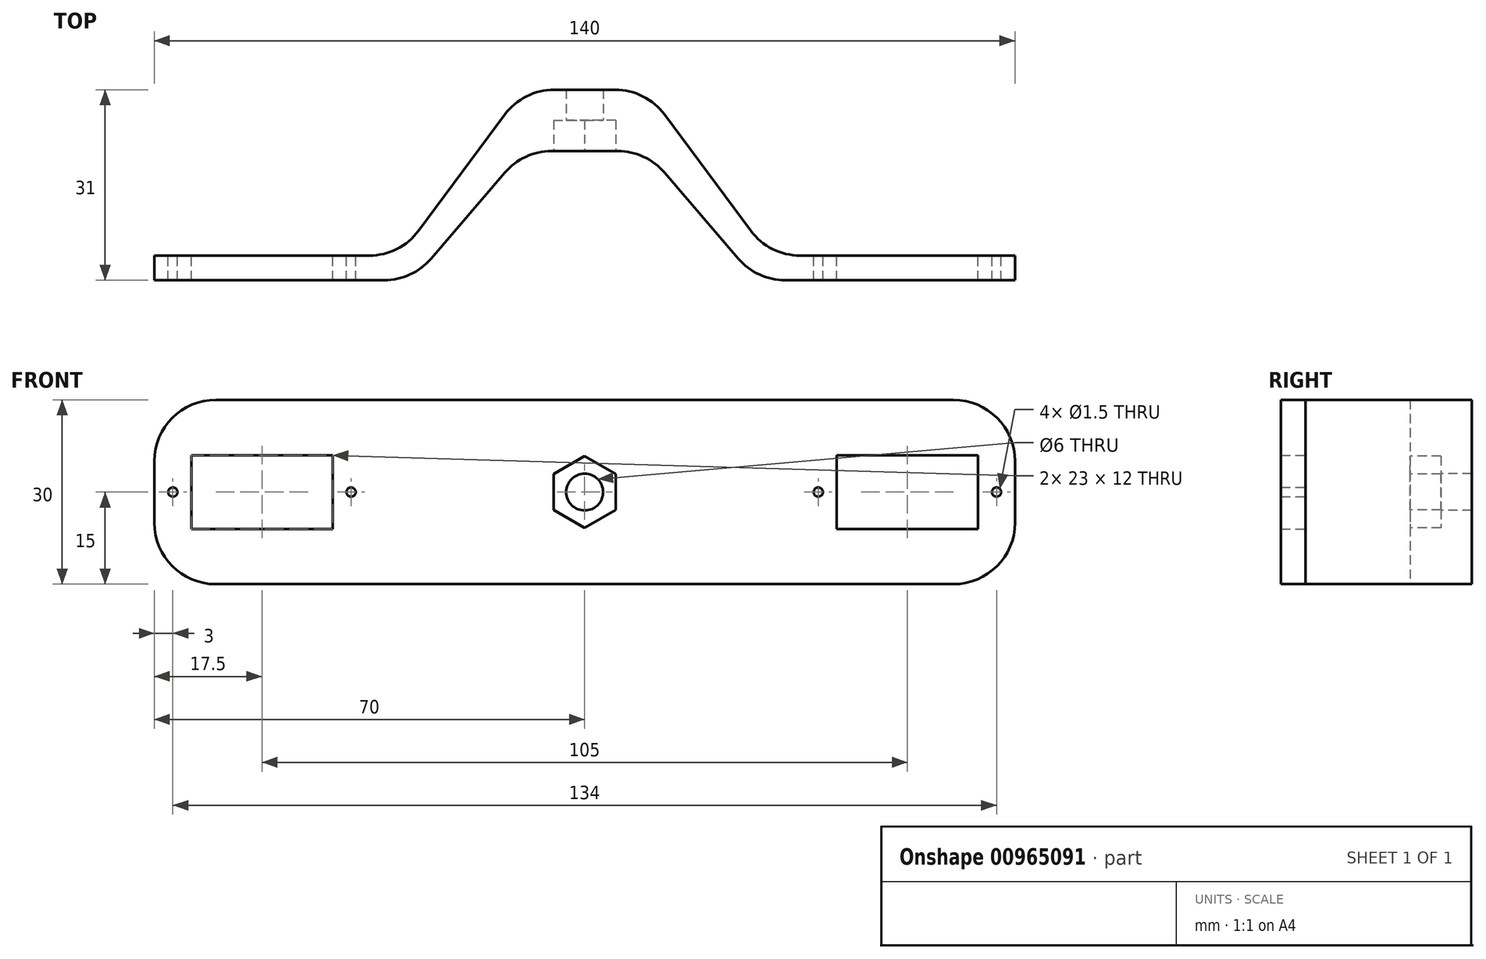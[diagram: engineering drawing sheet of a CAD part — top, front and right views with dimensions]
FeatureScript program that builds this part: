
annotation { "Feature Type Name" : "Feature", "Feature Type Description" : "" }
export const myFeature = defineFeature(function(context is Context, id is Id, definition is map)
    precondition{}
    {
        {
            var Q0;
            Q0=qCreatedBy(makeId("Top.planeOp"),FACE);
            var sketch = newSketch(context, id + "F0", { "sketchPlane" : qUnion([Q0])});
            skLineSegment(sketch, "E0", {"start": v(10, 31) * mm, "end": v(-10, 31) * mm});
            skLineSegment(sketch, "E1", {"start": v(-10, 31) * mm, "end": v(-30, 4) * mm});
            skLineSegment(sketch, "E2", {"start": v(-30, 4) * mm, "end": v(-70, 4) * mm});
            skLineSegment(sketch, "E3", {"start": v(-70, 4) * mm, "end": v(-70, 0) * mm});
            skLineSegment(sketch, "E4", {"start": v(70, 0) * mm, "end": v(70, 4) * mm});
            skLineSegment(sketch, "E5", {"start": v(70, 4) * mm, "end": v(30, 4) * mm});
            skLineSegment(sketch, "E6", {"start": v(30, 4) * mm, "end": v(10, 31) * mm});
            skLineSegment(sketch, "E7", {"start": v(-70, 0) * mm, "end": v(-28, 0) * mm});
            skLineSegment(sketch, "E8", {"start": v(-28, 0) * mm, "end": v(-10, 21) * mm});
            skLineSegment(sketch, "E9", {"start": v(-10, 21) * mm, "end": v(10, 21) * mm});
            skLineSegment(sketch, "E10", {"start": v(10, 21) * mm, "end": v(28, 0) * mm});
            skLineSegment(sketch, "E11", {"start": v(28, 0) * mm, "end": v(70, 0) * mm});
            skSolve(sketch);
        }
        {
            var Q0;
            Q0=makeQuery(id+"F0.imprint","IMPRINT",FACE,{"disambiguationData":[TD([[makeQuery(id+"F0.imprint","IMPRINT",EDGE,{"derivedFrom":sQuery(id+"F0.wireOp",EDGE,"E0")}),1.0]])]});
            extrude(context, id + "F1", {"entities" : qUnion([Q0]), "depth" : 30 * mm, "offsetDistance" : 25 * mm});
        }
        {
            var Q0;
            Q0=makeQuery(id+"F1.opExtrude","SWEPT_FACE",FACE,{"disambiguationData":[OSD([sQuery(id+"F0.wireOp",EDGE,"E5")])]});
            var sketch = newSketch(context, id + "F2", { "sketchPlane" : qUnion([Q0])});
            skLineSegment(sketch, "E12.bottom", {"start": v(64, 9) * mm, "end": v(41, 9) * mm});
            skLineSegment(sketch, "E12.top", {"start": v(64, 21) * mm, "end": v(41, 21) * mm});
            skLineSegment(sketch, "E12.left", {"start": v(64, 9) * mm, "end": v(64, 21) * mm});
            skLineSegment(sketch, "E12.right", {"start": v(41, 9) * mm, "end": v(41, 21) * mm});
            skLineSegment(sketch, "E13.bottom", {"start": v(-41, 9) * mm, "end": v(-64, 9) * mm});
            skLineSegment(sketch, "E13.top", {"start": v(-41, 21) * mm, "end": v(-64, 21) * mm});
            skLineSegment(sketch, "E13.left", {"start": v(-41, 9) * mm, "end": v(-41, 21) * mm});
            skLineSegment(sketch, "E13.right", {"start": v(-64, 9) * mm, "end": v(-64, 21) * mm});
            skCircle(sketch, "E14", {"center": v(67, 15) * mm, "radius": 0.75 * mm});
            skCircle(sketch, "E15", {"center": v(38, 15) * mm, "radius": 0.75 * mm});
            skCircle(sketch, "E16", {"center": v(-67, 15) * mm, "radius": 0.75 * mm});
            skCircle(sketch, "E17", {"center": v(-38, 15) * mm, "radius": 0.75 * mm});
            skSolve(sketch);
        }
        {
            var Q0;
            Q0=makeQuery(id+"F2.imprint","IMPRINT",FACE,{"disambiguationData":[TD([[makeQuery(id+"F2.imprint","IMPRINT",EDGE,{"derivedFrom":sQuery(id+"F2.wireOp",EDGE,"E12.bottom")}),-1.0]])]});
            var Q1;
            Q1=makeQuery(id+"F2.imprint","IMPRINT",FACE,{"disambiguationData":[TD([[makeQuery(id+"F2.imprint","IMPRINT",EDGE,{"derivedFrom":sQuery(id+"F2.wireOp",EDGE,"E13.bottom")}),-1.0]])]});
            var Q2;
            Q2=makeQuery(id+"F2.imprint","IMPRINT",FACE,{"disambiguationData":[TD([[makeQuery(id+"F2.imprint","IMPRINT",EDGE,{"derivedFrom":sQuery(id+"F2.wireOp",EDGE,"E17")}),1.0]])]});
            var Q3;
            Q3=makeQuery(id+"F2.imprint","IMPRINT",FACE,{"disambiguationData":[TD([[makeQuery(id+"F2.imprint","IMPRINT",EDGE,{"derivedFrom":sQuery(id+"F2.wireOp",EDGE,"E16")}),1.0]])]});
            var Q4;
            Q4=makeQuery(id+"F2.imprint","IMPRINT",FACE,{"disambiguationData":[TD([[makeQuery(id+"F2.imprint","IMPRINT",EDGE,{"derivedFrom":sQuery(id+"F2.wireOp",EDGE,"E15")}),1.0]])]});
            var Q5;
            Q5=makeQuery(id+"F2.imprint","IMPRINT",FACE,{"disambiguationData":[TD([[makeQuery(id+"F2.imprint","IMPRINT",EDGE,{"derivedFrom":sQuery(id+"F2.wireOp",EDGE,"E14")}),1.0]])]});
            extrude(context, id + "F3", {"entities" : qUnion([Q0, Q1, Q2, Q3, Q4, Q5]), "operationType" : NewBodyOperationType.REMOVE, "oppositeDirection" : true, "depth" : 25 * mm, "offsetDistance" : 25 * mm});
        }
        {
            var Q0;
            Q0=makeQuery(id+"F1.opExtrude","CAP_EDGE",EDGE,{"disambiguationData":[OSD([sQuery(id+"F0.wireOp",EDGE,"E3")])],"isStart":false});
            var Q1;
            Q1=makeQuery(id+"F1.opExtrude","CAP_EDGE",EDGE,{"disambiguationData":[OSD([sQuery(id+"F0.wireOp",EDGE,"E3")])],"isStart":true});
            var Q2;
            Q2=makeQuery(id+"F1.opExtrude","CAP_EDGE",EDGE,{"disambiguationData":[OSD([sQuery(id+"F0.wireOp",EDGE,"E4")])],"isStart":false});
            var Q3;
            Q3=makeQuery(id+"F1.opExtrude","CAP_EDGE",EDGE,{"disambiguationData":[OSD([sQuery(id+"F0.wireOp",EDGE,"E4")])],"isStart":true});
            var Q4;
            Q4=makeQuery(id+"F1.opExtrude","SWEPT_EDGE",EDGE,{"disambiguationData":[OSD([sQuery(id+"F0.wireOp",EDGE,"E5"),sQuery(id+"F0.wireOp",EDGE,"E6")])]});
            var Q5;
            Q5=makeQuery(id+"F1.opExtrude","SWEPT_EDGE",EDGE,{"disambiguationData":[OSD([sQuery(id+"F0.wireOp",EDGE,"E1"),sQuery(id+"F0.wireOp",EDGE,"E2")])]});
            var Q6;
            Q6=makeQuery(id+"F1.opExtrude","SWEPT_EDGE",EDGE,{"disambiguationData":[OSD([sQuery(id+"F0.wireOp",EDGE,"E0"),sQuery(id+"F0.wireOp",EDGE,"E1")])]});
            var Q7;
            Q7=makeQuery(id+"F1.opExtrude","SWEPT_EDGE",EDGE,{"disambiguationData":[OSD([sQuery(id+"F0.wireOp",EDGE,"E0"),sQuery(id+"F0.wireOp",EDGE,"E6")])]});
            var Q8;
            Q8=makeQuery(id+"F1.opExtrude","SWEPT_EDGE",EDGE,{"disambiguationData":[OSD([sQuery(id+"F0.wireOp",EDGE,"E7"),sQuery(id+"F0.wireOp",EDGE,"E8")])]});
            var Q9;
            Q9=makeQuery(id+"F1.opExtrude","SWEPT_EDGE",EDGE,{"disambiguationData":[OSD([sQuery(id+"F0.wireOp",EDGE,"E8"),sQuery(id+"F0.wireOp",EDGE,"E9")])]});
            var Q10;
            Q10=makeQuery(id+"F1.opExtrude","SWEPT_EDGE",EDGE,{"disambiguationData":[OSD([sQuery(id+"F0.wireOp",EDGE,"E9"),sQuery(id+"F0.wireOp",EDGE,"E10")])]});
            var Q11;
            Q11=makeQuery(id+"F1.opExtrude","SWEPT_EDGE",EDGE,{"disambiguationData":[OSD([sQuery(id+"F0.wireOp",EDGE,"E10"),sQuery(id+"F0.wireOp",EDGE,"E11")])]});
            fillet(context, id + "F4", {"entities" : qUnion([Q0, Q1, Q2, Q3, Q4, Q5, Q6, Q7, Q8, Q9, Q10, Q11]), "radius" : 10 * mm, "tangentPropagation" : true, "allowEdgeOverflow" : false});
        }
        {
            var Q0;
            Q0=makeQuery(id+"F1.opExtrude","SWEPT_FACE",FACE,{"disambiguationData":[OSD([sQuery(id+"F0.wireOp",EDGE,"E9")])]});
            var sketch = newSketch(context, id + "F5", { "sketchPlane" : qUnion([Q0])});
            skCircle(sketch, "E18", {"center": v(0, 15) * mm, "radius": 3 * mm});
            skCircle(sketch, "E19.cCircle", {"center": v(0, 15) * mm, "radius": 5.05 * mm, "construction": true});
            skLineSegment(sketch, "E19.0", {"start": v(5.05, 12.08) * mm, "end": v(0, 9.17) * mm});
            skLineSegment(sketch, "E19.1", {"start": v(0, 9.17) * mm, "end": v(-5.05, 12.08) * mm});
            skLineSegment(sketch, "E19.2", {"start": v(-5.05, 12.08) * mm, "end": v(-5.05, 17.92) * mm});
            skLineSegment(sketch, "E19.3", {"start": v(-5.05, 17.92) * mm, "end": v(0, 20.83) * mm});
            skLineSegment(sketch, "E19.4", {"start": v(0, 20.83) * mm, "end": v(5.05, 17.92) * mm});
            skLineSegment(sketch, "E19.5", {"start": v(5.05, 17.92) * mm, "end": v(5.05, 12.08) * mm});
            skPoint(sketch, "E19.0.midPoint", {"position": v(2.53, 10.63) * mm});
            skSolve(sketch);
        }
        {
            var Q0;
            Q0=makeQuery(id+"F5.imprint","IMPRINT",FACE,{"disambiguationData":[TD([[makeQuery(id+"F5.imprint","IMPRINT",EDGE,{"derivedFrom":sQuery(id+"F5.wireOp",EDGE,"E18")}),1.0]])]});
            extrude(context, id + "F6", {"entities" : qUnion([Q0]), "operationType" : NewBodyOperationType.REMOVE, "oppositeDirection" : true, "depth" : 25 * mm, "offsetDistance" : 25 * mm});
        }
        {
            var Q0;
            Q0=makeQuery(id+"F5.imprint","IMPRINT",FACE,{"disambiguationData":[TD([[makeQuery(id+"F5.imprint","IMPRINT",EDGE,{"derivedFrom":sQuery(id+"F5.wireOp",EDGE,"E18")}),-1.0]])]});
            var Q1;
            {var subQ0=sQuery(id+"F5.wireOp",EDGE,"BezBhqOi-Dq81-y19x-YtIC-0gsC98FfVjEG");var subQ1=sQuery(id+"F5.wireOp",EDGE,"ncgn8NgD-MM0d-W8xm-oQu1-WhMMswXOpPgE.bottom");var subQ2=makeQuery(id+"F5.imprint","INTERSECT",VERTEX,{"derivedFrom":[subQ1,subQ0]});Q1=makeQuery(id+"F5.imprint","IMPRINT",FACE,{"disambiguationData":[TD([[makeQuery(id+"F5.imprint","IMPRINT",EDGE,{"disambiguationData":[TD([[subQ2,-1.0]])],"derivedFrom":subQ1}),1.0]])]});}
            var Q2;
            {var subQ0=sQuery(id+"F5.wireOp",EDGE,"6shvffcE-fs8c-bkRR-tV69-GbnKZBFpZLUS");var subQ1=sQuery(id+"F5.wireOp",EDGE,"ncgn8NgD-MM0d-W8xm-oQu1-WhMMswXOpPgE.top");var subQ2=makeQuery(id+"F5.imprint","INTERSECT",VERTEX,{"derivedFrom":[subQ1,subQ0]});Q2=makeQuery(id+"F5.imprint","IMPRINT",FACE,{"disambiguationData":[TD([[makeQuery(id+"F5.imprint","IMPRINT",EDGE,{"disambiguationData":[TD([[subQ2,-1.0]])],"derivedFrom":subQ1}),-1.0]])]});}
            extrude(context, id + "F7", {"entities" : qUnion([Q0, Q1, Q2]), "operationType" : NewBodyOperationType.REMOVE, "oppositeDirection" : true, "depth" : 5 * mm, "offsetDistance" : 25 * mm});
        }
    });
